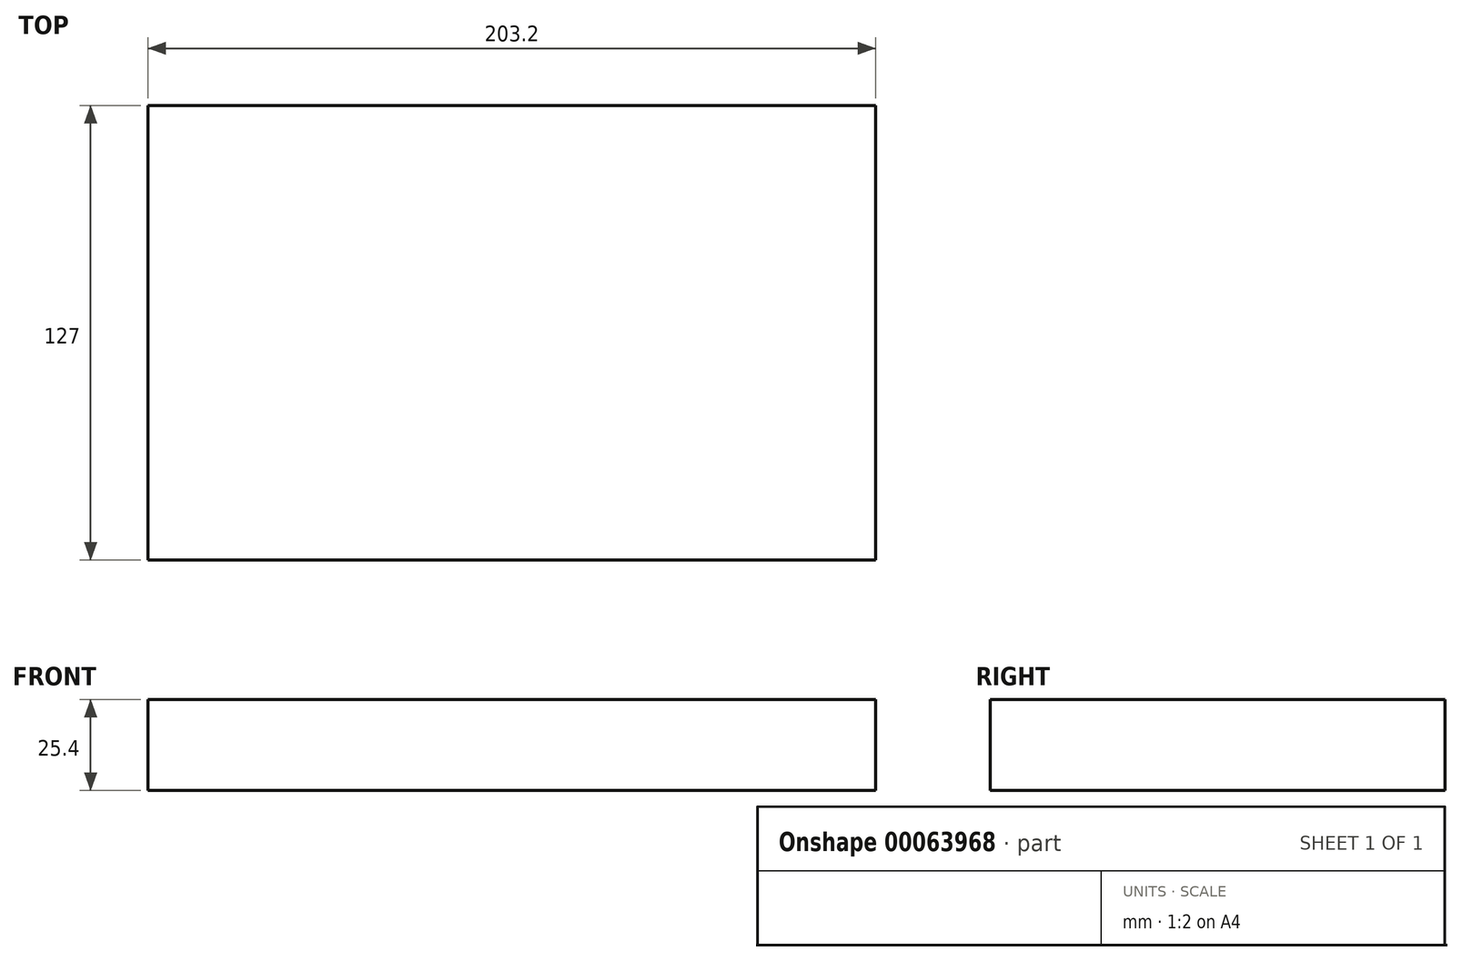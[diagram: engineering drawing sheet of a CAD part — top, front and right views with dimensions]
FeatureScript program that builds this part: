
annotation { "Feature Type Name" : "Feature", "Feature Type Description" : "" }
export const myFeature = defineFeature(function(context is Context, id is Id, definition is map)
    precondition{}
    {
        {
            var Q0;
            Q0=qCreatedBy(makeId("Top.planeOp"),FACE);
            var sketch = newSketch(context, id + "F0", { "sketchPlane" : qUnion([Q0])});
            skLineSegment(sketch, "E0.bottom", {"start": v(-29.87, 93.2) * mm, "end": v(173.33, 93.2) * mm});
            skLineSegment(sketch, "E0.top", {"start": v(-29.87, -33.8) * mm, "end": v(173.33, -33.8) * mm});
            skLineSegment(sketch, "E0.left", {"start": v(-29.87, 93.2) * mm, "end": v(-29.87, -33.8) * mm});
            skLineSegment(sketch, "E0.right", {"start": v(173.33, 93.2) * mm, "end": v(173.33, -33.8) * mm});
            skSolve(sketch);
        }
        {
            var Q0;
            Q0 = qSketchRegion(id + "F0", true);
            extrude(context, id + "F1", {"entities" : qUnion([Q0]), "depth" : 25.4 * mm});
        }
    });
